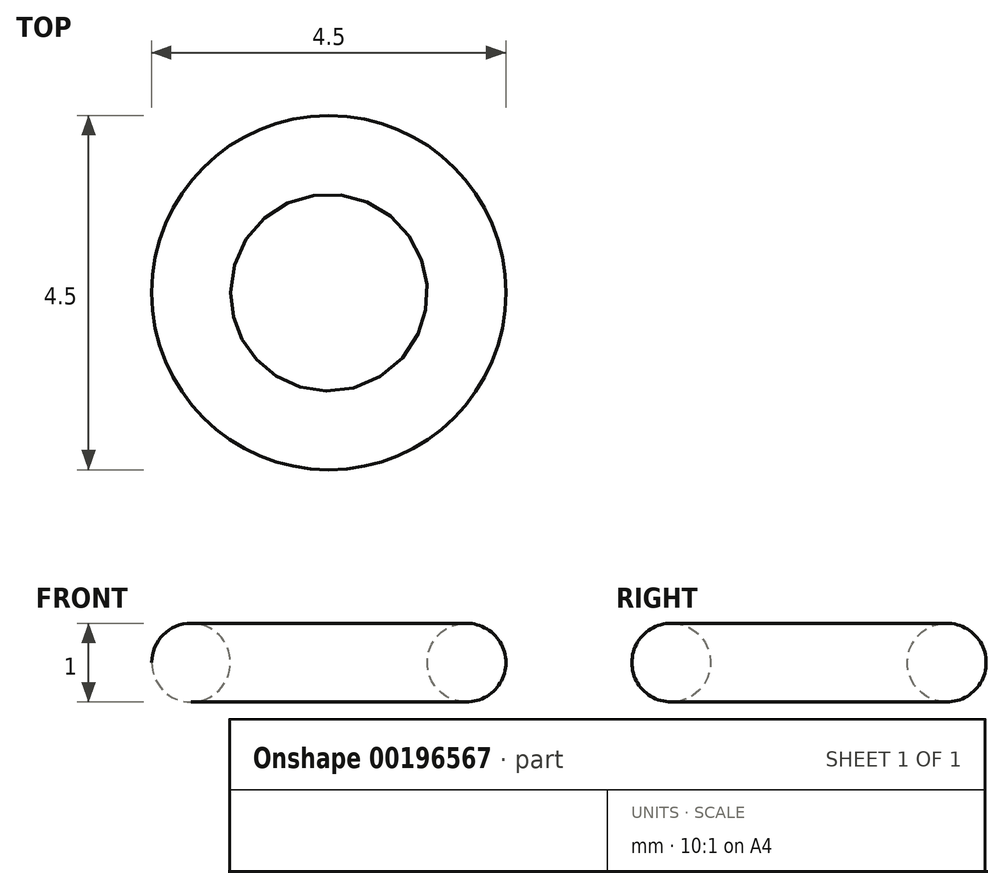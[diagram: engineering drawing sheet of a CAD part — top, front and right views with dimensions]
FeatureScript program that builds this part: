
annotation { "Feature Type Name" : "Feature", "Feature Type Description" : "" }
export const myFeature = defineFeature(function(context is Context, id is Id, definition is map)
    precondition{}
    {
        {
            var Q0;
            Q0=qCreatedBy(makeId("Front.planeOp"),FACE);
            var sketch = newSketch(context, id + "F0", { "sketchPlane" : qUnion([Q0])});
            skCircle(sketch, "E0", {"center": v(1.75, 0) * mm, "radius": 0.5 * mm});
            skLineSegment(sketch, "E1", {"start": v(0, 0) * mm, "end": v(0, 1.65) * mm, "construction": true});
            skSolve(sketch);
        }
        {
            var Q0;
            Q0=makeQuery(id+"F0.imprint","IMPRINT",FACE,{"disambiguationData":[TD([[makeQuery(id+"F0.imprint","IMPRINT",EDGE,{"derivedFrom":sQuery(id+"F0.wireOp",EDGE,"E0")}),1.0]])]});
            var Q1;
            Q1=sQuery(id+"F0.wireOp",EDGE,"E1");
            revolve(context, id + "F1", {"entities" : qUnion([Q0]), "axis" : qUnion([Q1]), "revolveType" : RevolveType.FULL});
        }
    });
